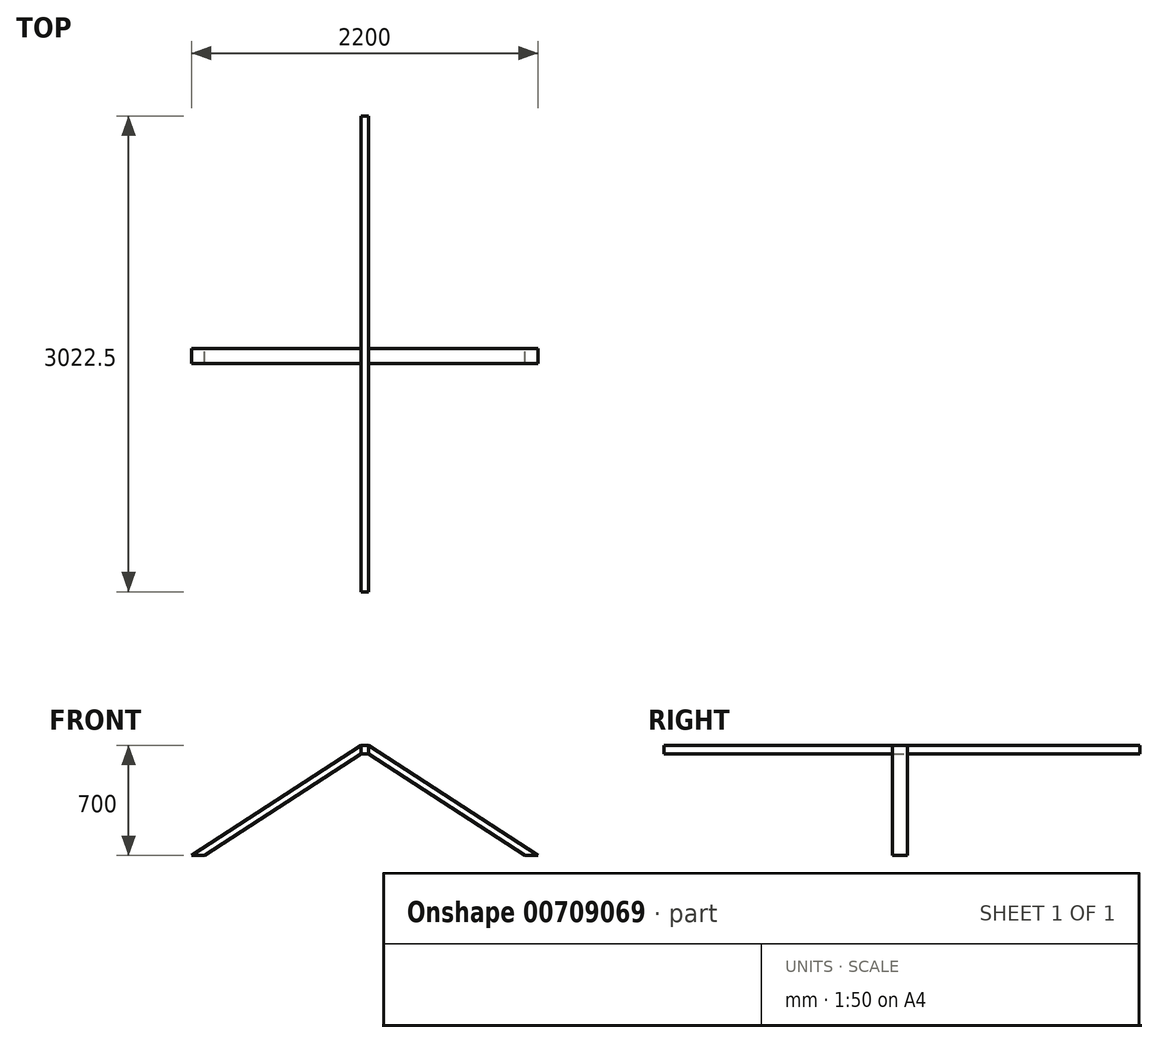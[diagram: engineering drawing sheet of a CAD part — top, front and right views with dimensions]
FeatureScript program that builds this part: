
annotation { "Feature Type Name" : "Feature", "Feature Type Description" : "" }
export const myFeature = defineFeature(function(context is Context, id is Id, definition is map)
    precondition{}
    {
        {
            var Q0;
            Q0=qCreatedBy(makeId("Front.planeOp"),FACE);
            var sketch = newSketch(context, id + "F0", { "sketchPlane" : qUnion([Q0])});
            skLineSegment(sketch, "E0.top", {"start": v(22.5, 291.2) * mm, "end": v(-22.5, 291.2) * mm});
            skLineSegment(sketch, "E1", {"start": v(-1100, -408.8) * mm, "end": v(-22.5, 291.2) * mm});
            skLineSegment(sketch, "E2", {"start": v(-22.5, 237.55) * mm, "end": v(-1017.4, -408.8) * mm});
            skLineSegment(sketch, "E3", {"start": v(-1017.4, -408.8) * mm, "end": v(-1100, -408.8) * mm});
            skLineSegment(sketch, "E4", {"start": v(22.5, 291.2) * mm, "end": v(1100, -408.8) * mm});
            skLineSegment(sketch, "E5", {"start": v(1017.4, -408.8) * mm, "end": v(22.5, 237.55) * mm});
            skLineSegment(sketch, "E6", {"start": v(22.5, 237.55) * mm, "end": v(22.5, 291.2) * mm});
            skLineSegment(sketch, "E7", {"start": v(1100, -408.8) * mm, "end": v(1017.4, -408.8) * mm});
            skLineSegment(sketch, "E8", {"start": v(-22.5, 291.2) * mm, "end": v(-22.5, 237.55) * mm});
            skLineSegment(sketch, "E9", {"start": v(22.5, 237.55) * mm, "end": v(-22.5, 237.55) * mm});
            skSolve(sketch);
        }
        {
            var Q0;
            Q0=makeQuery(id+"F0.imprint","IMPRINT",FACE,{"disambiguationData":[TD([[makeQuery(id+"F0.imprint","IMPRINT",EDGE,{"derivedFrom":sQuery(id+"F0.wireOp",EDGE,"E1")}),-1.0]])]});
            var Q1;
            Q1=makeQuery(id+"F0.imprint","IMPRINT",FACE,{"disambiguationData":[TD([[makeQuery(id+"F0.imprint","IMPRINT",EDGE,{"derivedFrom":sQuery(id+"F0.wireOp",EDGE,"E4")}),-1.0]])]});
            extrude(context, id + "F1", {"entities" : qUnion([Q0, Q1]), "depth" : 95 * mm, "offsetDistance" : 25 * mm});
        }
        {
            var Q0;
            Q0=makeQuery(id+"F0.imprint","IMPRINT",FACE,{"disambiguationData":[TD([[makeQuery(id+"F0.imprint","IMPRINT",EDGE,{"derivedFrom":sQuery(id+"F0.wireOp",EDGE,"E0.top")}),1.0]])]});
            extrude(context, id + "F2", {"entities" : qUnion([Q0]), "oppositeDirection" : true, "depth" : 1477.5 * mm, "offsetDistance" : 25 * mm});
        }
        {
            var Q0;
            Q0=makeQuery(id+"F0.imprint","IMPRINT",FACE,{"disambiguationData":[TD([[makeQuery(id+"F0.imprint","IMPRINT",EDGE,{"derivedFrom":sQuery(id+"F0.wireOp",EDGE,"E0.top")}),1.0]])]});
            extrude(context, id + "F3", {"entities" : qUnion([Q0]), "operationType" : NewBodyOperationType.ADD, "depth" : 1545 * mm, "offsetDistance" : 25 * mm});
        }
    });
